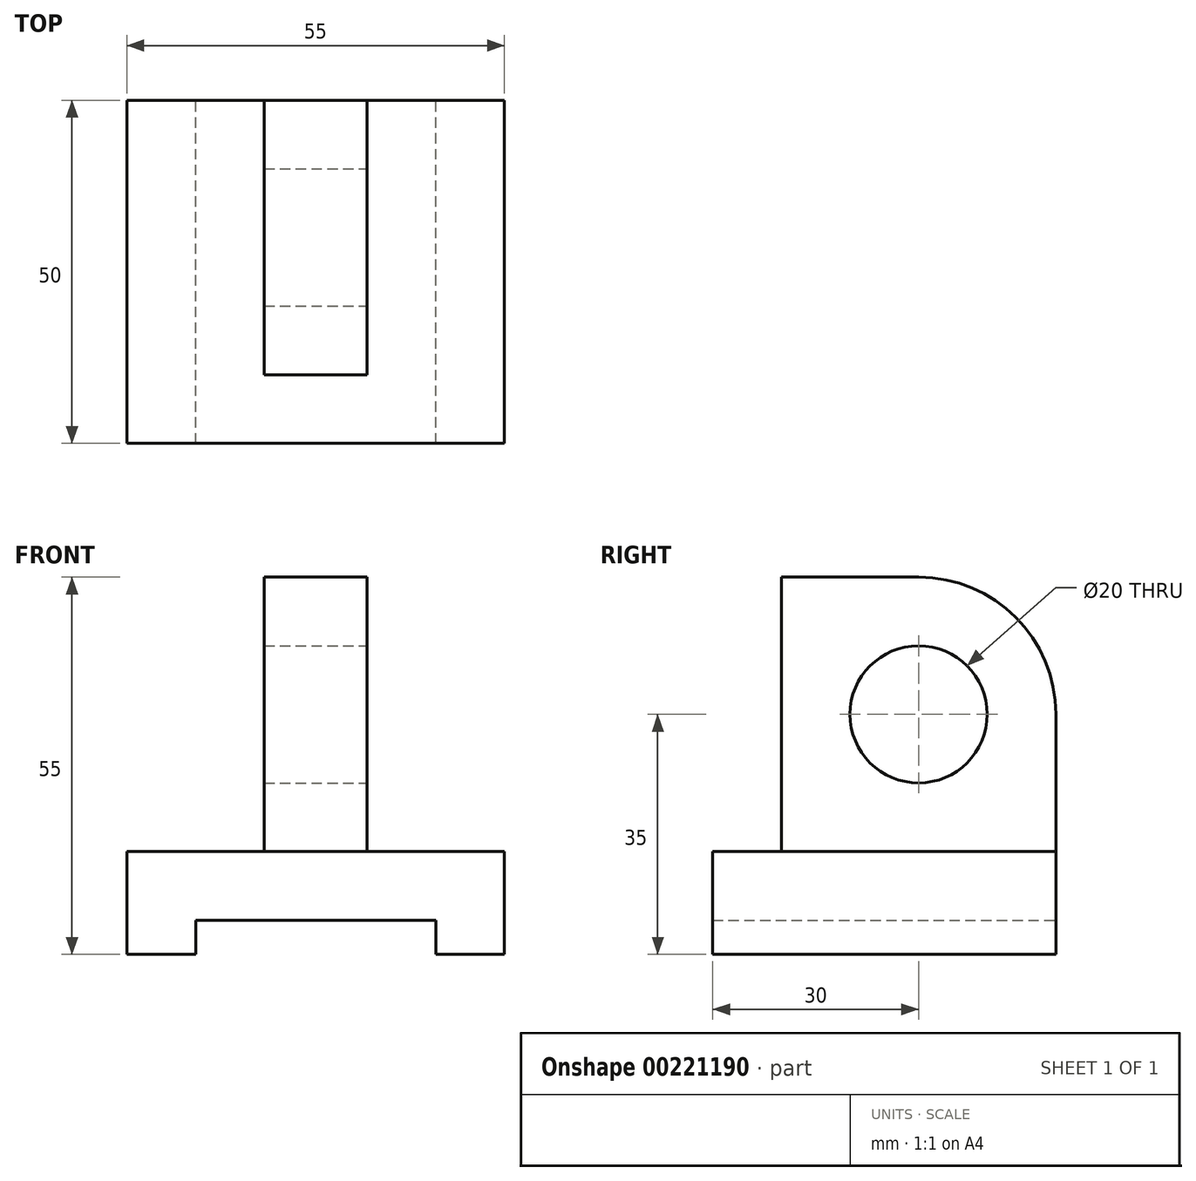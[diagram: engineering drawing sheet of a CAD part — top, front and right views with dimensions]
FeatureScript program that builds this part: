
annotation { "Feature Type Name" : "Feature", "Feature Type Description" : "" }
export const myFeature = defineFeature(function(context is Context, id is Id, definition is map)
    precondition{}
    {
        {
            var Q0;
            Q0=qCreatedBy(makeId("Front.planeOp"),FACE);
            var sketch = newSketch(context, id + "F0", { "sketchPlane" : qUnion([Q0])});
            skLineSegment(sketch, "E0", {"start": v(-27.5, 7.5) * mm, "end": v(27.5, 7.5) * mm});
            skLineSegment(sketch, "E1", {"start": v(27.5, 7.5) * mm, "end": v(27.5, -7.5) * mm});
            skLineSegment(sketch, "E2", {"start": v(27.5, -7.5) * mm, "end": v(17.5, -7.5) * mm});
            skLineSegment(sketch, "E3", {"start": v(17.5, -7.5) * mm, "end": v(17.5, -2.5) * mm});
            skLineSegment(sketch, "E4", {"start": v(17.5, -2.5) * mm, "end": v(-17.5, -2.5) * mm});
            skLineSegment(sketch, "E5", {"start": v(-17.5, -2.5) * mm, "end": v(-17.5, -7.5) * mm});
            skLineSegment(sketch, "E6", {"start": v(-17.5, -7.5) * mm, "end": v(-27.5, -7.5) * mm});
            skLineSegment(sketch, "E7", {"start": v(-27.5, -7.5) * mm, "end": v(-27.5, 7.5) * mm});
            skSolve(sketch);
        }
        {
            var Q0;
            Q0=makeQuery(id+"F0.imprint","IMPRINT",FACE,{"disambiguationData":[TD([[makeQuery(id+"F0.imprint","IMPRINT",EDGE,{"derivedFrom":sQuery(id+"F0.wireOp",EDGE,"E0")}),-1.0]])]});
            extrude(context, id + "F1", {"entities" : qUnion([Q0]), "endBound" : BoundingType.SYMMETRIC, "depth" : 50 * mm});
        }
        {
            var Q0;
            Q0=qCreatedBy(makeId("Right.planeOp"),FACE);
            var sketch = newSketch(context, id + "F2", { "sketchPlane" : qUnion([Q0])});
            skLineSegment(sketch, "E8.0", {"start": v(-15, 7.5) * mm, "end": v(25, 7.5) * mm});
            skLineSegment(sketch, "E9", {"start": v(25, 7.5) * mm, "end": v(25, 47.5) * mm});
            skLineSegment(sketch, "E10", {"start": v(25, 47.5) * mm, "end": v(-15, 47.5) * mm});
            skLineSegment(sketch, "E11", {"start": v(-15, 47.5) * mm, "end": v(-15, 7.5) * mm});
            skPoint(sketch, "E12.orphan", {"position": v(-25, 7.5) * mm});
            skSolve(sketch);
        }
        {
            var Q0;
            Q0=makeQuery(id+"F2.imprint","IMPRINT",FACE,{"disambiguationData":[TD([[makeQuery(id+"F2.imprint","IMPRINT",EDGE,{"derivedFrom":sQuery(id+"F2.wireOp",EDGE,"E8.0")}),1.0]])]});
            extrude(context, id + "F3", {"entities" : qUnion([Q0]), "operationType" : NewBodyOperationType.ADD, "endBound" : BoundingType.SYMMETRIC, "depth" : 15 * mm});
        }
        {
            var Q0;
            Q0=makeQuery(id+"F3.opExtrude","CAP_FACE",FACE,{"disambiguationData":[OSD([sQuery(id+"F2.wireOp",EDGE,"E8.0"),sQuery(id+"F2.wireOp",EDGE,"E9"),sQuery(id+"F2.wireOp",EDGE,"E10"),sQuery(id+"F2.wireOp",EDGE,"E11")])],"isStart":false});
            var sketch = newSketch(context, id + "F4", { "sketchPlane" : qUnion([Q0])});
            skCircle(sketch, "E13", {"center": v(5, 27.5) * mm, "radius": 10 * mm});
            skPoint(sketch, "E13.centerSnap0", {"position": v(-15, 27.5) * mm});
            skPoint(sketch, "E13.centerSnap1", {"position": v(5, 7.5) * mm});
            skSolve(sketch);
        }
        {
            var Q0;
            Q0 = qSketchRegion(id + "F4", true);
            var Q1;
            Q1=makeQuery(id+"F3.opExtrude","CAP_FACE",FACE,{"disambiguationData":[OSD([sQuery(id+"F2.wireOp",EDGE,"E8.0"),sQuery(id+"F2.wireOp",EDGE,"E9"),sQuery(id+"F2.wireOp",EDGE,"E10"),sQuery(id+"F2.wireOp",EDGE,"E11")])],"isStart":true});
            extrude(context, id + "F5", {"entities" : qUnion([Q0]), "operationType" : NewBodyOperationType.REMOVE, "endBound" : BoundingType.UP_TO_SURFACE, "oppositeDirection" : true, "endBoundEntityFace" : qUnion([Q1]), "depth" : 25 * mm});
        }
        {
            var Q0;
            Q0=makeQuery(id+"F3.opExtrude","SWEPT_EDGE",EDGE,{"disambiguationData":[OSD([sQuery(id+"F2.wireOp",EDGE,"E9"),sQuery(id+"F2.wireOp",EDGE,"E10")])]});
            fillet(context, id + "F6", {"entities" : qUnion([Q0]), "radius" : 20 * mm, "tangentPropagation" : true, "allowEdgeOverflow" : false});
        }
    });
